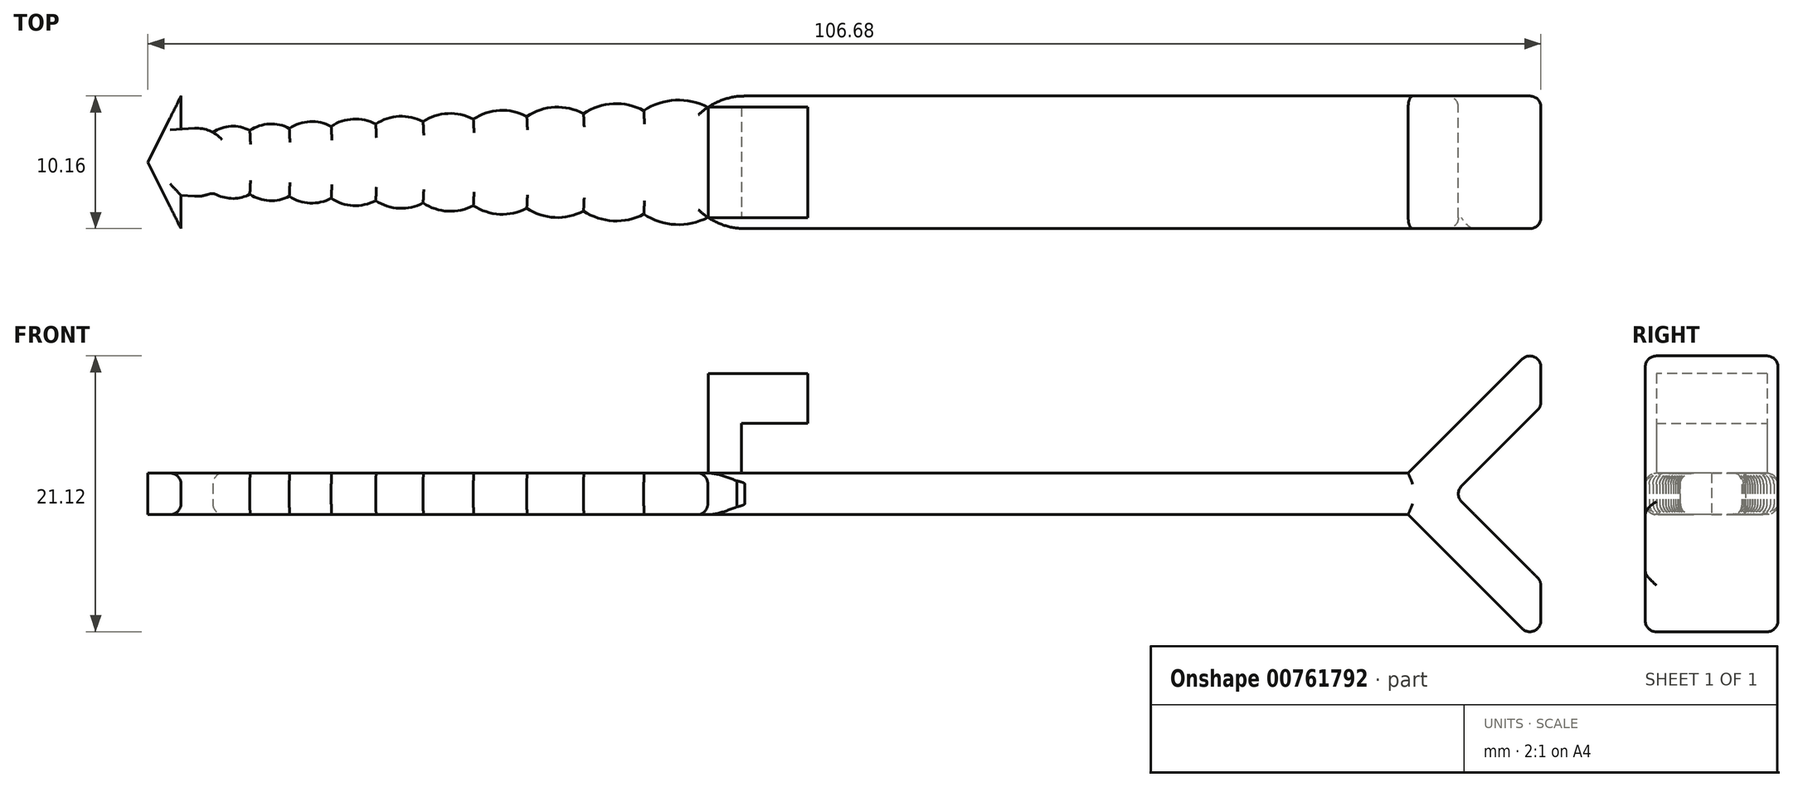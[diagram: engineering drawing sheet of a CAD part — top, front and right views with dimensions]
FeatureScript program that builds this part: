
annotation { "Feature Type Name" : "Feature", "Feature Type Description" : "" }
export const myFeature = defineFeature(function(context is Context, id is Id, definition is map)
    precondition{}
    {
        {
            var Q0;
            Q0=qCreatedBy(makeId("Top.planeOp"),FACE);
            var sketch = newSketch(context, id + "F0", { "sketchPlane" : qUnion([Q0])});
            skLineSegment(sketch, "E0", {"start": v(45.72, 5.08) * mm, "end": v(96.52, 5.08) * mm});
            skLineSegment(sketch, "E1", {"start": v(45.72, -5.08) * mm, "end": v(96.52, -5.08) * mm});
            skLineSegment(sketch, "E2", {"start": v(0, 0) * mm, "end": v(2.54, 5.08) * mm});
            skLineSegment(sketch, "E3.MirrorCS", {"start": v(0, 0) * mm, "end": v(2.54, -5.08) * mm});
            skLineSegment(sketch, "E4", {"start": v(2.54, 5.08) * mm, "end": v(2.54, 2.54) * mm});
            skPoint(sketch, "E5.startSnap0", {"position": v(1.27, 2.54) * mm});
            skLineSegment(sketch, "E6.trimOffspring", {"start": v(2.54, -2.54) * mm, "end": v(2.54, -5.08) * mm});
            skPoint(sketch, "E7.orphan", {"position": v(1.27, -2.54) * mm});
            skLineSegment(sketch, "E8", {"start": v(2.54, -2.54) * mm, "end": v(3.58, -2.6) * mm});
            skLineSegment(sketch, "E9", {"start": v(2.54, 2.54) * mm, "end": v(3.58, 2.6) * mm});
            skArc(sketch, "E10", {"start": v(42.88, -4.21) * mm, "mid": v(44.24, -4.86) * mm, "end": v(45.72, -5.08) * mm});
            skArc(sketch, "E11", {"start": v(37.98, -3.96) * mm, "mid": v(40.4, -4.77) * mm, "end": v(42.88, -4.21) * mm});
            skArc(sketch, "E12", {"start": v(33.36, -3.73) * mm, "mid": v(35.64, -4.49) * mm, "end": v(37.98, -3.96) * mm});
            skArc(sketch, "E13", {"start": v(29.02, -3.51) * mm, "mid": v(31.16, -4.22) * mm, "end": v(33.36, -3.73) * mm});
            skArc(sketch, "E14", {"start": v(24.93, -3.3) * mm, "mid": v(26.95, -3.98) * mm, "end": v(29.02, -3.51) * mm});
            skArc(sketch, "E15", {"start": v(21.08, -3.11) * mm, "mid": v(22.98, -3.74) * mm, "end": v(24.93, -3.3) * mm});
            skArc(sketch, "E16", {"start": v(17.45, -2.93) * mm, "mid": v(19.24, -3.52) * mm, "end": v(21.08, -3.11) * mm});
            skArc(sketch, "E17", {"start": v(14.04, -2.76) * mm, "mid": v(15.72, -3.32) * mm, "end": v(17.45, -2.93) * mm});
            skArc(sketch, "E18", {"start": v(10.83, -2.6) * mm, "mid": v(12.41, -3.12) * mm, "end": v(14.04, -2.76) * mm});
            skArc(sketch, "E19", {"start": v(7.8, -2.44) * mm, "mid": v(9.3, -2.94) * mm, "end": v(10.83, -2.6) * mm});
            skArc(sketch, "E20", {"start": v(4.96, -2.3) * mm, "mid": v(6.37, -2.76) * mm, "end": v(7.8, -2.44) * mm});
            skArc(sketch, "E21", {"start": v(3.58, -2.6) * mm, "mid": v(4.3, -2.55) * mm, "end": v(4.96, -2.3) * mm});
            skArc(sketch, "E22.trimOffspring", {"start": v(4.96, 2.3) * mm, "mid": v(4.3, 2.55) * mm, "end": v(3.58, 2.6) * mm});
            skArc(sketch, "E23.trimOffspring", {"start": v(7.8, 2.44) * mm, "mid": v(6.37, 2.76) * mm, "end": v(4.96, 2.3) * mm});
            skArc(sketch, "E24.trimOffspring", {"start": v(10.83, 2.6) * mm, "mid": v(9.3, 2.94) * mm, "end": v(7.8, 2.44) * mm});
            skArc(sketch, "E25.trimOffspring", {"start": v(14.04, 2.76) * mm, "mid": v(12.41, 3.12) * mm, "end": v(10.83, 2.6) * mm});
            skArc(sketch, "E26.trimOffspring", {"start": v(17.45, 2.93) * mm, "mid": v(15.72, 3.32) * mm, "end": v(14.04, 2.76) * mm});
            skArc(sketch, "E27.trimOffspring", {"start": v(21.08, 3.11) * mm, "mid": v(19.24, 3.52) * mm, "end": v(17.45, 2.93) * mm});
            skArc(sketch, "E28.trimOffspring", {"start": v(24.93, 3.3) * mm, "mid": v(22.98, 3.74) * mm, "end": v(21.08, 3.11) * mm});
            skArc(sketch, "E29.trimOffspring", {"start": v(29.02, 3.51) * mm, "mid": v(26.95, 3.98) * mm, "end": v(24.93, 3.3) * mm});
            skArc(sketch, "E30.trimOffspring", {"start": v(33.36, 3.73) * mm, "mid": v(31.16, 4.22) * mm, "end": v(29.02, 3.51) * mm});
            skArc(sketch, "E31.trimOffspring", {"start": v(37.98, 3.96) * mm, "mid": v(35.64, 4.49) * mm, "end": v(33.36, 3.73) * mm});
            skArc(sketch, "E32.trimOffspring", {"start": v(42.88, 4.21) * mm, "mid": v(40.4, 4.77) * mm, "end": v(37.98, 3.96) * mm});
            skArc(sketch, "E33.trimOffspring", {"start": v(45.72, 5.08) * mm, "mid": v(44.24, 4.86) * mm, "end": v(42.88, 4.21) * mm});
            skLineSegment(sketch, "E34.trimOffspring", {"start": v(45.12, 5.04) * mm, "end": v(45.72, 5.08) * mm});
            skLineSegment(sketch, "E35.trimOffspring", {"start": v(45.12, -5.04) * mm, "end": v(45.72, -5.08) * mm});
            skLineSegment(sketch, "E36", {"start": v(96.52, 5.08) * mm, "end": v(96.52, -5.08) * mm});
            skSolve(sketch);
        }
        {
            var Q0;
            {var subQ1=sQuery(id+"F0.wireOp",EDGE,"E0");Q0=makeQuery(id+"F0.imprint","IMPRINT",FACE,{"disambiguationData":[TD([[makeQuery(id+"F0.imprint","IMPRINT",EDGE,{"derivedFrom":subQ1}),-1.0]])]});}
            extrude(context, id + "F1", {"entities" : qUnion([Q0]), "depth" : 3.17 * mm, "offsetDistance" : 25.4 * mm});
        }
        {
            var Q0;
            Q0=makeQuery(id+"F1.opExtrude","CAP_EDGE",EDGE,{"disambiguationData":[OSD([sQuery(id+"F0.wireOp",EDGE,"E11")])],"isStart":false});
            var Q1;
            Q1=makeQuery(id+"F1.opExtrude","CAP_EDGE",EDGE,{"disambiguationData":[OSD([sQuery(id+"F0.wireOp",EDGE,"E12")])],"isStart":false});
            var Q2;
            Q2=makeQuery(id+"F1.opExtrude","CAP_EDGE",EDGE,{"disambiguationData":[OSD([sQuery(id+"F0.wireOp",EDGE,"E13")])],"isStart":false});
            var Q3;
            Q3=makeQuery(id+"F1.opExtrude","CAP_EDGE",EDGE,{"disambiguationData":[OSD([sQuery(id+"F0.wireOp",EDGE,"E13")])],"isStart":true});
            var Q4;
            Q4=makeQuery(id+"F1.opExtrude","CAP_EDGE",EDGE,{"disambiguationData":[OSD([sQuery(id+"F0.wireOp",EDGE,"E12")])],"isStart":true});
            var Q5;
            Q5=makeQuery(id+"F1.opExtrude","CAP_EDGE",EDGE,{"disambiguationData":[OSD([sQuery(id+"F0.wireOp",EDGE,"E11")])],"isStart":true});
            var Q6;
            Q6=makeQuery(id+"F1.opExtrude","CAP_EDGE",EDGE,{"disambiguationData":[OSD([sQuery(id+"F0.wireOp",EDGE,"E14")])],"isStart":true});
            var Q7;
            Q7=makeQuery(id+"F1.opExtrude","CAP_EDGE",EDGE,{"disambiguationData":[OSD([sQuery(id+"F0.wireOp",EDGE,"E15")])],"isStart":true});
            var Q8;
            Q8=makeQuery(id+"F1.opExtrude","CAP_EDGE",EDGE,{"disambiguationData":[OSD([sQuery(id+"F0.wireOp",EDGE,"E14")])],"isStart":false});
            var Q9;
            Q9=makeQuery(id+"F1.opExtrude","CAP_EDGE",EDGE,{"disambiguationData":[OSD([sQuery(id+"F0.wireOp",EDGE,"E15")])],"isStart":false});
            var Q10;
            Q10=makeQuery(id+"F1.opExtrude","CAP_EDGE",EDGE,{"disambiguationData":[OSD([sQuery(id+"F0.wireOp",EDGE,"E16")])],"isStart":false});
            var Q11;
            Q11=makeQuery(id+"F1.opExtrude","CAP_EDGE",EDGE,{"disambiguationData":[OSD([sQuery(id+"F0.wireOp",EDGE,"E16")])],"isStart":true});
            var Q12;
            Q12=makeQuery(id+"F1.opExtrude","CAP_EDGE",EDGE,{"disambiguationData":[OSD([sQuery(id+"F0.wireOp",EDGE,"E17")])],"isStart":false});
            var Q13;
            Q13=makeQuery(id+"F1.opExtrude","CAP_EDGE",EDGE,{"disambiguationData":[OSD([sQuery(id+"F0.wireOp",EDGE,"E17")])],"isStart":true});
            var Q14;
            Q14=makeQuery(id+"F1.opExtrude","CAP_EDGE",EDGE,{"disambiguationData":[OSD([sQuery(id+"F0.wireOp",EDGE,"E18")])],"isStart":false});
            var Q15;
            Q15=makeQuery(id+"F1.opExtrude","CAP_EDGE",EDGE,{"disambiguationData":[OSD([sQuery(id+"F0.wireOp",EDGE,"E18")])],"isStart":true});
            var Q16;
            Q16=makeQuery(id+"F1.opExtrude","CAP_EDGE",EDGE,{"disambiguationData":[OSD([sQuery(id+"F0.wireOp",EDGE,"E19")])],"isStart":true});
            var Q17;
            Q17=makeQuery(id+"F1.opExtrude","CAP_EDGE",EDGE,{"disambiguationData":[OSD([sQuery(id+"F0.wireOp",EDGE,"E19")])],"isStart":false});
            var Q18;
            Q18=makeQuery(id+"F1.opExtrude","CAP_EDGE",EDGE,{"disambiguationData":[OSD([sQuery(id+"F0.wireOp",EDGE,"E20")])],"isStart":false});
            var Q19;
            Q19=makeQuery(id+"F1.opExtrude","CAP_EDGE",EDGE,{"disambiguationData":[OSD([sQuery(id+"F0.wireOp",EDGE,"E20")])],"isStart":true});
            var Q20;
            Q20=makeQuery(id+"F1.opExtrude","SWEPT_FACE",FACE,{"disambiguationData":[OSD([sQuery(id+"F0.wireOp",EDGE,"E21")])]});
            var Q21;
            Q21=makeQuery(id+"F1.opExtrude","CAP_EDGE",EDGE,{"disambiguationData":[OSD([sQuery(id+"F0.wireOp",EDGE,"E6.trimOffspring")])],"isStart":false});
            var Q22;
            Q22=makeQuery(id+"F1.opExtrude","CAP_EDGE",EDGE,{"disambiguationData":[OSD([sQuery(id+"F0.wireOp",EDGE,"E6.trimOffspring")])],"isStart":true});
            var Q23;
            Q23=makeQuery(id+"F1.opExtrude","CAP_EDGE",EDGE,{"disambiguationData":[OSD([sQuery(id+"F0.wireOp",EDGE,"E4")])],"isStart":false});
            var Q24;
            Q24=makeQuery(id+"F1.opExtrude","CAP_EDGE",EDGE,{"disambiguationData":[OSD([sQuery(id+"F0.wireOp",EDGE,"E4")])],"isStart":true});
            var Q25;
            Q25=makeQuery(id+"F1.opExtrude","CAP_EDGE",EDGE,{"disambiguationData":[OSD([sQuery(id+"F0.wireOp",EDGE,"E0")])],"isStart":false});
            var Q26;
            Q26=makeQuery(id+"F1.opExtrude","CAP_EDGE",EDGE,{"disambiguationData":[OSD([sQuery(id+"F0.wireOp",EDGE,"E0")])],"isStart":true});
            var Q27;
            Q27=makeQuery(id+"F1.opExtrude","CAP_EDGE",EDGE,{"disambiguationData":[OSD([sQuery(id+"F0.wireOp",EDGE,"E1")])],"isStart":false});
            var Q28;
            Q28=makeQuery(id+"F1.opExtrude","CAP_EDGE",EDGE,{"disambiguationData":[OSD([sQuery(id+"F0.wireOp",EDGE,"E1")])],"isStart":true});
            var Q29;
            Q29=makeQuery(id+"F1.opExtrude","CAP_EDGE",EDGE,{"disambiguationData":[OSD([sQuery(id+"F0.wireOp",EDGE,"QIR4PNLN-daRh-Gd68-Y0mB-JoI59tZlPrwv")])],"isStart":false});
            var Q30;
            Q30=makeQuery(id+"F1.opExtrude","CAP_EDGE",EDGE,{"disambiguationData":[OSD([sQuery(id+"F0.wireOp",EDGE,"QIR4PNLN-daRh-Gd68-Y0mB-JoI59tZlPrwv")])],"isStart":true});
            var Q31;
            Q31=makeQuery(id+"F1.opExtrude","CAP_EDGE",EDGE,{"disambiguationData":[OSD([sQuery(id+"F0.wireOp",EDGE,"CrDNqOtH-8dSI-nxnW-ycpq-Ji4sb4s0cmW3")])],"isStart":false});
            var Q32;
            Q32=makeQuery(id+"F1.opExtrude","CAP_EDGE",EDGE,{"disambiguationData":[OSD([sQuery(id+"F0.wireOp",EDGE,"CrDNqOtH-8dSI-nxnW-ycpq-Ji4sb4s0cmW3")])],"isStart":true});
            var Q33;
            Q33=makeQuery(id+"F1.opExtrude","CAP_EDGE",EDGE,{"disambiguationData":[OSD([sQuery(id+"F0.wireOp",EDGE,"EUHHyH1w-Ft7Z-Wq75-WS98-GZo82FLjrV1i")])],"isStart":false});
            var Q34;
            Q34=makeQuery(id+"F1.opExtrude","CAP_EDGE",EDGE,{"disambiguationData":[OSD([sQuery(id+"F0.wireOp",EDGE,"EUHHyH1w-Ft7Z-Wq75-WS98-GZo82FLjrV1i")])],"isStart":true});
            var Q35;
            Q35=makeQuery(id+"F1.opExtrude","CAP_EDGE",EDGE,{"disambiguationData":[OSD([sQuery(id+"F0.wireOp",EDGE,"7J9Orzlo-GbWV-PXDs-phhW-Sn9F6xIrcmfW")])],"isStart":false});
            var Q36;
            Q36=makeQuery(id+"F1.opExtrude","CAP_EDGE",EDGE,{"disambiguationData":[OSD([sQuery(id+"F0.wireOp",EDGE,"7J9Orzlo-GbWV-PXDs-phhW-Sn9F6xIrcmfW")])],"isStart":true});
            var Q37;
            Q37=makeQuery(id+"F1.opExtrude","CAP_EDGE",EDGE,{"disambiguationData":[OSD([sQuery(id+"F0.wireOp",EDGE,"ze2sdPND-qN4k-zJ9I-Zpfl-PBVmMqmbpBkt")])],"isStart":true});
            var Q38;
            Q38=makeQuery(id+"F1.opExtrude","CAP_EDGE",EDGE,{"disambiguationData":[OSD([sQuery(id+"F0.wireOp",EDGE,"ze2sdPND-qN4k-zJ9I-Zpfl-PBVmMqmbpBkt")])],"isStart":false});
            var Q39;
            Q39=makeQuery(id+"F1.opExtrude","CAP_EDGE",EDGE,{"disambiguationData":[OSD([sQuery(id+"F0.wireOp",EDGE,"uj2xfkP0-VGXR-pQvU-L6DS-siw4YtUn9gLI")])],"isStart":false});
            var Q40;
            Q40=makeQuery(id+"F1.opExtrude","CAP_EDGE",EDGE,{"disambiguationData":[OSD([sQuery(id+"F0.wireOp",EDGE,"uj2xfkP0-VGXR-pQvU-L6DS-siw4YtUn9gLI")])],"isStart":true});
            var Q41;
            Q41=makeQuery(id+"F1.opExtrude","CAP_EDGE",EDGE,{"disambiguationData":[OSD([sQuery(id+"F0.wireOp",EDGE,"E32.trimOffspring")])],"isStart":false});
            var Q42;
            Q42=makeQuery(id+"F1.opExtrude","CAP_EDGE",EDGE,{"disambiguationData":[OSD([sQuery(id+"F0.wireOp",EDGE,"E31.trimOffspring")])],"isStart":false});
            var Q43;
            Q43=makeQuery(id+"F1.opExtrude","CAP_EDGE",EDGE,{"disambiguationData":[OSD([sQuery(id+"F0.wireOp",EDGE,"E30.trimOffspring")])],"isStart":false});
            var Q44;
            Q44=makeQuery(id+"F1.opExtrude","CAP_EDGE",EDGE,{"disambiguationData":[OSD([sQuery(id+"F0.wireOp",EDGE,"E29.trimOffspring")])],"isStart":false});
            var Q45;
            Q45=makeQuery(id+"F1.opExtrude","CAP_EDGE",EDGE,{"disambiguationData":[OSD([sQuery(id+"F0.wireOp",EDGE,"E28.trimOffspring")])],"isStart":false});
            var Q46;
            Q46=makeQuery(id+"F1.opExtrude","CAP_EDGE",EDGE,{"disambiguationData":[OSD([sQuery(id+"F0.wireOp",EDGE,"E27.trimOffspring")])],"isStart":false});
            var Q47;
            Q47=makeQuery(id+"F1.opExtrude","CAP_EDGE",EDGE,{"disambiguationData":[OSD([sQuery(id+"F0.wireOp",EDGE,"E26.trimOffspring")])],"isStart":false});
            var Q48;
            Q48=makeQuery(id+"F1.opExtrude","CAP_EDGE",EDGE,{"disambiguationData":[OSD([sQuery(id+"F0.wireOp",EDGE,"E25.trimOffspring")])],"isStart":false});
            var Q49;
            Q49=makeQuery(id+"F1.opExtrude","CAP_EDGE",EDGE,{"disambiguationData":[OSD([sQuery(id+"F0.wireOp",EDGE,"E24.trimOffspring")])],"isStart":false});
            var Q50;
            Q50=makeQuery(id+"F1.opExtrude","CAP_EDGE",EDGE,{"disambiguationData":[OSD([sQuery(id+"F0.wireOp",EDGE,"E23.trimOffspring")])],"isStart":false});
            var Q51;
            Q51=makeQuery(id+"F1.opExtrude","CAP_EDGE",EDGE,{"disambiguationData":[OSD([sQuery(id+"F0.wireOp",EDGE,"E24.trimOffspring")])],"isStart":true});
            var Q52;
            Q52=makeQuery(id+"F1.opExtrude","CAP_EDGE",EDGE,{"disambiguationData":[OSD([sQuery(id+"F0.wireOp",EDGE,"E25.trimOffspring")])],"isStart":true});
            var Q53;
            Q53=makeQuery(id+"F1.opExtrude","CAP_EDGE",EDGE,{"disambiguationData":[OSD([sQuery(id+"F0.wireOp",EDGE,"E23.trimOffspring")])],"isStart":true});
            var Q54;
            Q54=makeQuery(id+"F1.opExtrude","CAP_EDGE",EDGE,{"disambiguationData":[OSD([sQuery(id+"F0.wireOp",EDGE,"E26.trimOffspring")])],"isStart":true});
            var Q55;
            Q55=makeQuery(id+"F1.opExtrude","CAP_EDGE",EDGE,{"disambiguationData":[OSD([sQuery(id+"F0.wireOp",EDGE,"E27.trimOffspring")])],"isStart":true});
            var Q56;
            Q56=makeQuery(id+"F1.opExtrude","CAP_EDGE",EDGE,{"disambiguationData":[OSD([sQuery(id+"F0.wireOp",EDGE,"E28.trimOffspring")])],"isStart":true});
            var Q57;
            Q57=makeQuery(id+"F1.opExtrude","CAP_EDGE",EDGE,{"disambiguationData":[OSD([sQuery(id+"F0.wireOp",EDGE,"E29.trimOffspring")])],"isStart":true});
            var Q58;
            Q58=makeQuery(id+"F1.opExtrude","CAP_EDGE",EDGE,{"disambiguationData":[OSD([sQuery(id+"F0.wireOp",EDGE,"E30.trimOffspring")])],"isStart":true});
            var Q59;
            Q59=makeQuery(id+"F1.opExtrude","CAP_EDGE",EDGE,{"disambiguationData":[OSD([sQuery(id+"F0.wireOp",EDGE,"E31.trimOffspring")])],"isStart":true});
            var Q60;
            Q60=makeQuery(id+"F1.opExtrude","CAP_EDGE",EDGE,{"disambiguationData":[OSD([sQuery(id+"F0.wireOp",EDGE,"E32.trimOffspring")])],"isStart":true});
            fillet(context, id + "F2", {"entities" : qUnion([Q0, Q1, Q2, Q3, Q4, Q5, Q6, Q7, Q8, Q9, Q10, Q11, Q12, Q13, Q14, Q15, Q16, Q17, Q18, Q19, Q20, Q21, Q22, Q23, Q24, Q25, Q26, Q27, Q28, Q29, Q30, Q31, Q32, Q33, Q34, Q35, Q36, Q37, Q38, Q39, Q40, Q41, Q42, Q43, Q44, Q45, Q46, Q47, Q48, Q49, Q50, Q51, Q52, Q53, Q54, Q55, Q56, Q57, Q58, Q59, Q60]), "radius" : 0.84 * mm, "tangentPropagation" : true, "allowEdgeOverflow" : false});
        }
        {
            var Q0;
            Q0=makeQuery(id+"F1.opExtrude","CAP_FACE",FACE,{"disambiguationData":[OSD([sQuery(id+"F0.wireOp",EDGE,"E0"),sQuery(id+"F0.wireOp",EDGE,"E1"),sQuery(id+"F0.wireOp",EDGE,"QIR4PNLN-daRh-Gd68-Y0mB-JoI59tZlPrwv"),sQuery(id+"F0.wireOp",EDGE,"CrDNqOtH-8dSI-nxnW-ycpq-Ji4sb4s0cmW3"),sQuery(id+"F0.wireOp",EDGE,"EUHHyH1w-Ft7Z-Wq75-WS98-GZo82FLjrV1i"),sQuery(id+"F0.wireOp",EDGE,"7J9Orzlo-GbWV-PXDs-phhW-Sn9F6xIrcmfW"),sQuery(id+"F0.wireOp",EDGE,"ze2sdPND-qN4k-zJ9I-Zpfl-PBVmMqmbpBkt"),sQuery(id+"F0.wireOp",EDGE,"uj2xfkP0-VGXR-pQvU-L6DS-siw4YtUn9gLI"),sQuery(id+"F0.wireOp",EDGE,"E2"),sQuery(id+"F0.wireOp",EDGE,"E3.MirrorCS"),sQuery(id+"F0.wireOp",EDGE,"E4"),sQuery(id+"F0.wireOp",EDGE,"E6.trimOffspring"),sQuery(id+"F0.wireOp",EDGE,"E8"),sQuery(id+"F0.wireOp",EDGE,"E9"),sQuery(id+"F0.wireOp",EDGE,"E10"),sQuery(id+"F0.wireOp",EDGE,"E11"),sQuery(id+"F0.wireOp",EDGE,"E12"),sQuery(id+"F0.wireOp",EDGE,"E13"),sQuery(id+"F0.wireOp",EDGE,"E14"),sQuery(id+"F0.wireOp",EDGE,"E15"),sQuery(id+"F0.wireOp",EDGE,"E16"),sQuery(id+"F0.wireOp",EDGE,"E17"),sQuery(id+"F0.wireOp",EDGE,"E18"),sQuery(id+"F0.wireOp",EDGE,"E19"),sQuery(id+"F0.wireOp",EDGE,"E20"),sQuery(id+"F0.wireOp",EDGE,"E21"),sQuery(id+"F0.wireOp",EDGE,"E22.trimOffspring"),sQuery(id+"F0.wireOp",EDGE,"E23.trimOffspring"),sQuery(id+"F0.wireOp",EDGE,"E24.trimOffspring"),sQuery(id+"F0.wireOp",EDGE,"E25.trimOffspring"),sQuery(id+"F0.wireOp",EDGE,"E26.trimOffspring"),sQuery(id+"F0.wireOp",EDGE,"E27.trimOffspring"),sQuery(id+"F0.wireOp",EDGE,"E28.trimOffspring"),sQuery(id+"F0.wireOp",EDGE,"E29.trimOffspring"),sQuery(id+"F0.wireOp",EDGE,"E30.trimOffspring"),sQuery(id+"F0.wireOp",EDGE,"E31.trimOffspring"),sQuery(id+"F0.wireOp",EDGE,"E32.trimOffspring"),sQuery(id+"F0.wireOp",EDGE,"E33.trimOffspring"),sQuery(id+"F0.wireOp",EDGE,"E34.trimOffspring"),sQuery(id+"F0.wireOp",EDGE,"E35.trimOffspring")])],"isStart":false});
            var sketch = newSketch(context, id + "F3", { "sketchPlane" : qUnion([Q0])});
            skLineSegment(sketch, "E37.bottom", {"start": v(42.92, 4.24) * mm, "end": v(45.46, 4.24) * mm});
            skLineSegment(sketch, "E37.top", {"start": v(42.92, -4.24) * mm, "end": v(45.46, -4.24) * mm});
            skLineSegment(sketch, "E37.left", {"start": v(42.92, 4.24) * mm, "end": v(42.92, -4.24) * mm});
            skLineSegment(sketch, "E37.right", {"start": v(45.46, 4.24) * mm, "end": v(45.46, -4.24) * mm});
            skSolve(sketch);
        }
        {
            var Q0;
            Q0=makeQuery(id+"F3.imprint","IMPRINT",FACE,{"disambiguationData":[TD([[makeQuery(id+"F3.imprint","IMPRINT",EDGE,{"derivedFrom":sQuery(id+"F3.wireOp",EDGE,"E37.bottom")}),1.0]])]});
            extrude(context, id + "F4", {"entities" : qUnion([Q0]), "operationType" : NewBodyOperationType.ADD, "depth" : 7.62 * mm, "offsetDistance" : 25.4 * mm});
        }
        {
            var Q0;
            Q0=makeQuery(id+"F4.opExtrude","SWEPT_FACE",FACE,{"disambiguationData":[OSD([sQuery(id+"F3.wireOp",EDGE,"E37.right")])]});
            var sketch = newSketch(context, id + "F5", { "sketchPlane" : qUnion([Q0])});
            skLineSegment(sketch, "E38.bottom", {"start": v(-4.24, 10.8) * mm, "end": v(4.24, 10.8) * mm});
            skLineSegment(sketch, "E38.top", {"start": v(-4.24, 6.99) * mm, "end": v(4.24, 6.99) * mm});
            skLineSegment(sketch, "E38.left", {"start": v(-4.24, 10.8) * mm, "end": v(-4.24, 6.99) * mm});
            skLineSegment(sketch, "E38.right", {"start": v(4.24, 10.8) * mm, "end": v(4.24, 6.99) * mm});
            skSolve(sketch);
        }
        {
            var Q0;
            Q0=makeQuery(id+"F5.imprint","IMPRINT",FACE,{"disambiguationData":[TD([[makeQuery(id+"F5.imprint","IMPRINT",EDGE,{"derivedFrom":sQuery(id+"F5.wireOp",EDGE,"E38.bottom")}),1.0]])]});
            extrude(context, id + "F6", {"entities" : qUnion([Q0]), "operationType" : NewBodyOperationType.ADD, "depth" : 5.08 * mm, "offsetDistance" : 25.4 * mm});
        }
        {
            var Q0;
            Q0=qCreatedBy(makeId("Front.planeOp"),FACE);
            var sketch = newSketch(context, id + "F7", { "sketchPlane" : qUnion([Q0])});
            skLineSegment(sketch, "E39", {"start": v(96.52, 0) * mm, "end": v(106.68, -10.16) * mm});
            skLineSegment(sketch, "E40", {"start": v(106.68, -10.16) * mm, "end": v(106.68, -5.08) * mm});
            skLineSegment(sketch, "E41", {"start": v(106.68, -5.08) * mm, "end": v(100.01, 1.59) * mm});
            skLineSegment(sketch, "E42.MirrorCS", {"start": v(96.52, 3.17) * mm, "end": v(106.68, 13.33) * mm});
            skLineSegment(sketch, "E43.MirrorCS", {"start": v(106.68, 13.33) * mm, "end": v(106.68, 8.25) * mm});
            skLineSegment(sketch, "E44.MirrorCS", {"start": v(106.68, 8.26) * mm, "end": v(100.01, 1.59) * mm});
            skLineSegment(sketch, "E45", {"start": v(96.52, 3.17) * mm, "end": v(96.52, 0) * mm});
            skSolve(sketch);
        }
        {
            var Q0;
            Q0=makeQuery(id+"F7.imprint","IMPRINT",FACE,{"disambiguationData":[TD([[makeQuery(id+"F7.imprint","IMPRINT",EDGE,{"derivedFrom":sQuery(id+"F7.wireOp",EDGE,"E39")}),1.0]])]});
            extrude(context, id + "F8", {"entities" : qUnion([Q0]), "operationType" : NewBodyOperationType.ADD, "depth" : 5.08 * mm, "offsetDistance" : 25.4 * mm});
        }
        {
            var Q0;
            Q0=makeQuery(id+"F8.opExtrude","CAP_FACE",FACE,{"disambiguationData":[OSD([sQuery(id+"F7.wireOp",EDGE,"E39"),sQuery(id+"F7.wireOp",EDGE,"E40"),sQuery(id+"F7.wireOp",EDGE,"E41"),sQuery(id+"F7.wireOp",EDGE,"E42.MirrorCS"),sQuery(id+"F7.wireOp",EDGE,"E43.MirrorCS"),sQuery(id+"F7.wireOp",EDGE,"E44.MirrorCS"),sQuery(id+"F7.wireOp",EDGE,"E45")])],"isStart":true});
            extrude(context, id + "F9", {"entities" : qUnion([Q0]), "operationType" : NewBodyOperationType.ADD, "depth" : 5.08 * mm, "offsetDistance" : 25.4 * mm});
        }
        {
            var Q0;
            Q0=makeQuery(id+"F9.opExtrude","CAP_EDGE",EDGE,{"disambiguationData":[OSD([sQuery(id+"F7.wireOp",EDGE,"E42.MirrorCS")])],"isStart":false});
            var Q1;
            Q1=makeQuery(id+"F9.opExtrude","CAP_EDGE",EDGE,{"disambiguationData":[OSD([sQuery(id+"F7.wireOp",EDGE,"E43.MirrorCS")])],"isStart":false});
            var Q2;
            Q2=makeQuery(id+"F9.opExtrude","CAP_EDGE",EDGE,{"disambiguationData":[OSD([sQuery(id+"F7.wireOp",EDGE,"E44.MirrorCS")])],"isStart":false});
            var Q3;
            Q3=makeQuery(id+"F9.opExtrude","CAP_EDGE",EDGE,{"disambiguationData":[OSD([sQuery(id+"F7.wireOp",EDGE,"E41")])],"isStart":false});
            var Q4;
            Q4=makeQuery(id+"F9.opExtrude","CAP_EDGE",EDGE,{"disambiguationData":[OSD([sQuery(id+"F7.wireOp",EDGE,"E40")])],"isStart":false});
            var Q5;
            Q5=makeQuery(id+"F9.opExtrude","CAP_EDGE",EDGE,{"disambiguationData":[OSD([sQuery(id+"F7.wireOp",EDGE,"E39")])],"isStart":false});
            var Q6;
            {var subQ0=sQuery(id+"F7.wireOp",EDGE,"E43.MirrorCS");var subQ1=sQuery(id+"F7.wireOp",EDGE,"E42.MirrorCS");Q6=makeQuery(id+"F9.boolean.opBoolean","MERGE",EDGE,{"derivedFrom":[makeQuery(id+"F8.opExtrude","SWEPT_EDGE",EDGE,{"disambiguationData":[OSD([subQ1,subQ0])]}),makeQuery(id+"F9.opExtrude","SWEPT_EDGE",EDGE,{"disambiguationData":[OSD([subQ1,subQ0])]})]});}
            var Q7;
            {var subQ0=sQuery(id+"F7.wireOp",EDGE,"E44.MirrorCS");var subQ1=sQuery(id+"F7.wireOp",EDGE,"E43.MirrorCS");Q7=makeQuery(id+"F9.boolean.opBoolean","MERGE",EDGE,{"derivedFrom":[makeQuery(id+"F8.opExtrude","SWEPT_EDGE",EDGE,{"disambiguationData":[OSD([subQ1,subQ0])]}),makeQuery(id+"F9.opExtrude","SWEPT_EDGE",EDGE,{"disambiguationData":[OSD([subQ1,subQ0])]})]});}
            var Q8;
            {var subQ0=sQuery(id+"F7.wireOp",EDGE,"E44.MirrorCS");var subQ1=sQuery(id+"F7.wireOp",EDGE,"E41");Q8=makeQuery(id+"F9.boolean.opBoolean","MERGE",EDGE,{"derivedFrom":[makeQuery(id+"F8.opExtrude","SWEPT_EDGE",EDGE,{"disambiguationData":[OSD([subQ1,subQ0])]}),makeQuery(id+"F9.opExtrude","SWEPT_EDGE",EDGE,{"disambiguationData":[OSD([subQ1,subQ0])]})]});}
            var Q9;
            {var subQ0=sQuery(id+"F7.wireOp",EDGE,"E41");var subQ1=sQuery(id+"F7.wireOp",EDGE,"E40");Q9=makeQuery(id+"F9.boolean.opBoolean","MERGE",EDGE,{"derivedFrom":[makeQuery(id+"F8.opExtrude","SWEPT_EDGE",EDGE,{"disambiguationData":[OSD([subQ1,subQ0])]}),makeQuery(id+"F9.opExtrude","SWEPT_EDGE",EDGE,{"disambiguationData":[OSD([subQ1,subQ0])]})]});}
            var Q10;
            {var subQ0=sQuery(id+"F7.wireOp",EDGE,"E40");var subQ1=sQuery(id+"F7.wireOp",EDGE,"E39");Q10=makeQuery(id+"F9.boolean.opBoolean","MERGE",EDGE,{"derivedFrom":[makeQuery(id+"F8.opExtrude","SWEPT_EDGE",EDGE,{"disambiguationData":[OSD([subQ1,subQ0])]}),makeQuery(id+"F9.opExtrude","SWEPT_EDGE",EDGE,{"disambiguationData":[OSD([subQ1,subQ0])]})]});}
            var Q11;
            Q11=makeQuery(id+"F8.opExtrude","CAP_EDGE",EDGE,{"disambiguationData":[OSD([sQuery(id+"F7.wireOp",EDGE,"E44.MirrorCS")])],"isStart":false});
            var Q12;
            Q12=makeQuery(id+"F8.opExtrude","CAP_EDGE",EDGE,{"disambiguationData":[OSD([sQuery(id+"F7.wireOp",EDGE,"E43.MirrorCS")])],"isStart":false});
            var Q13;
            Q13=makeQuery(id+"F8.opExtrude","CAP_EDGE",EDGE,{"disambiguationData":[OSD([sQuery(id+"F7.wireOp",EDGE,"E39")])],"isStart":false});
            var Q14;
            Q14=makeQuery(id+"F8.opExtrude","CAP_EDGE",EDGE,{"disambiguationData":[OSD([sQuery(id+"F7.wireOp",EDGE,"E40")])],"isStart":false});
            var Q15;
            Q15=makeQuery(id+"F8.opExtrude","CAP_EDGE",EDGE,{"disambiguationData":[OSD([sQuery(id+"F7.wireOp",EDGE,"E42.MirrorCS")])],"isStart":false});
            fillet(context, id + "F10", {"entities" : qUnion([Q0, Q1, Q2, Q3, Q4, Q5, Q6, Q7, Q8, Q9, Q10, Q11, Q12, Q13, Q14, Q15]), "radius" : 0.84 * mm, "tangentPropagation" : true, "allowEdgeOverflow" : false});
        }
    });
